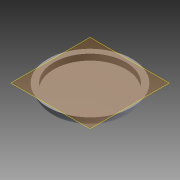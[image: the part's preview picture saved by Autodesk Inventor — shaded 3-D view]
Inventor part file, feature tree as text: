
AUTODESK INVENTOR PART (.ipt)
format: ipt  version: 2014 (Build 180170000, 170)  size: 118,272 bytes
history: native  units: mm
features: sketch x3, plane x1, loft x1, fillet x1, extrude x1
ambient origin geometry x8: Origin, YZ Plane, XZ Plane, XY Plane, X Axis, Y Axis, Z Axis, Center Point
bodies: Solid1 (feature_tree)
feature tree (7):
  sketch  "Sketch1"  dims[d0=120.0mm d1=20.0mm d2=140.0mm]
  plane  "Work Plane1"
  loft  "Loft1"
  fillet  "Fillet1"  Radius=140.0mm
  extrude  "Extrusion1"  TaperAngle=0.0deg  [1 undecoded]
  sketch  "Sketch2"  dims[d3=0.0mm d4=90.0deg d5=0.0mm d6=90.0deg]
  sketch  "Sketch3"  dims[d7=20.0mm d8=120.0mm d9=10.0mm d10=0.0mm]
note: 1 required parameter value undecoded (feature->parameter linkage not recoverable at this tier; creation-order binding heuristic only, values carry confidence <= 0.55)
